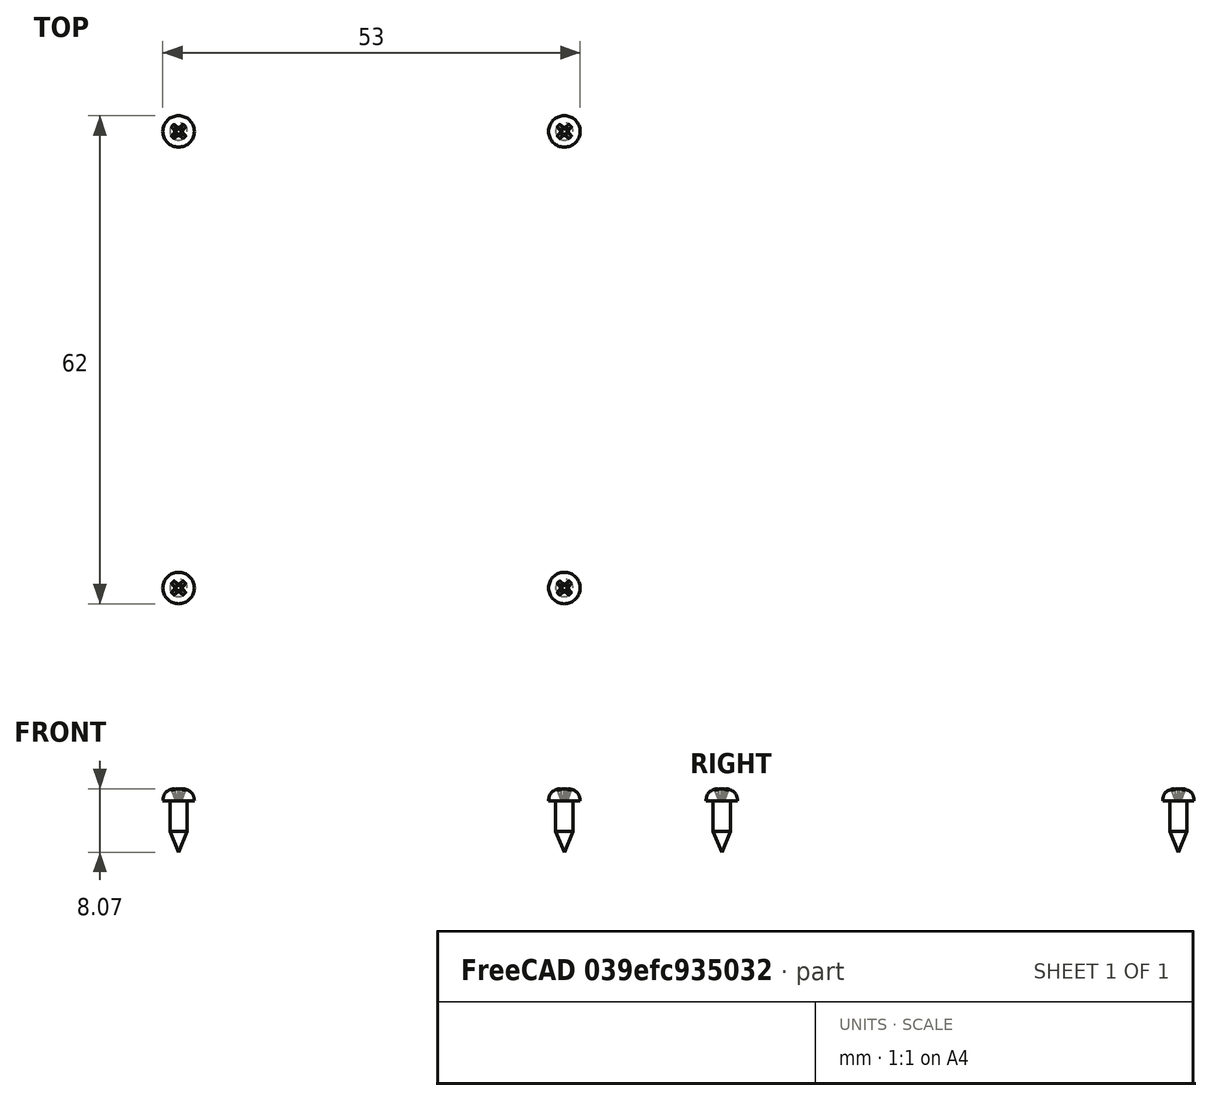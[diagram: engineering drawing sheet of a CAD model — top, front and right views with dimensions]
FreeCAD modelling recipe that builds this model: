
FCSTD DOCUMENT  (FreeCAD 1.0R39319 (Git))
Label: Assy_RaspberryPi5_carrier
License: All rights reserved
LicenseURL: https://en.wikipedia.org/wiki/All_rights_reserved
objects: TechDraw::DrawViewBalloon×6, Part::FeaturePython×4, TechDraw::DrawProjGroupItem×4, App::DocumentObjectGroup×3, TechDraw::DrawViewDimension×3, App::Link×2, TechDraw::DrawSVGTemplate×2, TechDraw::DrawPage×2, PartDesign::CoordinateSystem×1, App::FeaturePython×1, App::Part×1, Spreadsheet::Sheet×1, TechDraw::DrawViewSpreadsheet×1, TechDraw::DrawProjGroup×1
note: 11 computed .brp shape members not serialized (recipe doc carries the construction recipe); baked Part::Feature solids carry a one-line shape summary decoded from their .brp
EXTERNAL_REF file=../../Part/Print/Pi5_Carrier_vertical_3mm.FCStd obj=LCS_1
EXTERNAL_REF file=../../Part/Print/Pi5_Carrier_vertical_3mm.FCStd obj=Part
EXTERNAL_REF file=../../Part/Print/Pi5_Carrier_vertical_3mm.FCStd obj=pi5_att
EXTERNAL_REF file=../../Part/Purchase/RaspberryPi5.FCStd obj=LCS_1
EXTERNAL_REF file=../../Part/Purchase/RaspberryPi5.FCStd obj=RP_004882_DD___Pi_5_Mechanical_Reference_3D_model_Iss1

FEATURE [App::DocumentObjectGroup] Parts
FEATURE [PartDesign::CoordinateSystem] LCS_Origin
  AttacherType = Attacher::AttachEngine3D
  AttachmentSupport = -> [X_Axis]
  MapMode = 2
FEATURE [App::DocumentObjectGroup] Constraints
FEATURE [App::FeaturePython] Variables  # WARN: FeaturePython — macro-defined, semantics opaque (R4)
  Type = App::PropertyContainer
FEATURE [App::DocumentObjectGroup] Configurations
FEATURE [App::Link] Pi5_Carrier_vertical_3mm
  AttachedBy = #LCS_1
  AttachedTo = Parent Assembly#LCS_Origin
  LinkedObject = -> <external ../../Part/Print/Pi5_Carrier_vertical_3mm.FCStd>#Part
  SolverId = Asm4EE
  expr: Placement = LCS_Origin.Placement * AttachmentOffset * Pi5_Carrier_vertical_3mm#LCS_1.Placement ^ -1
FEATURE [App::Link] RP_004882_DD___Pi_5_Mechanical_Reference_3D_model_Iss1  label="RP-004882-DD - Pi 5 Mechanical Reference 3D model Iss1"
  AttachedBy = #LCS_1
  AttachedTo = Pi5_Carrier_vertical_3mm#pi5_att
  AttachmentOffset = pos=(0,0,0) rot=(0,0,1;3.14159rad)
  LinkPlacement = pos=(76,1,5.4) rot=(-0.57735,0.57735,0.57735;4.18879rad)
  LinkedObject = -> <external ../../Part/Purchase/RaspberryPi5.FCStd>#RP_004882_DD___Pi_5_Mechanical_Reference_3D_model_Iss1
  Placement = pos=(76,1,5.4) rot=(-0.57735,0.57735,0.57735;4.18879rad)
  SolverId = Asm4EE
  expr: Placement = Pi5_Carrier_vertical_3mm.Placement * Pi5_Carrier_vertical_3mm#pi5_att.Placement * AttachmentOffset * RaspberryPi5#LCS_1.Placement ^ -1
FEATURE [Part::FeaturePython] Screw  label="ST2.2x6.5-Screw"  # WARN: FeaturePython — macro-defined, semantics opaque (R4)
  BaseObject = -> Pi5_Carrier_vertical_3mm [Body.Fillet001.Edge193]
  Diameter = 1
  Invert = false
  LeftHanded = false
  Length = 1
  LengthCustom = 6.5
  MatchOuter = false
  Offset = 1.4
  OffsetAngle = 0
  Placement = pos=(51.5,40,6.9) rot=(0,0,1;0rad)
  Thread = false
  Type = 81
FEATURE [Part::FeaturePython] Screw001  label="ST2.2x6.5-Screw004"  # WARN: FeaturePython — macro-defined, semantics opaque (R4)
  BaseObject = -> Pi5_Carrier_vertical_3mm [Body.Fillet001.Edge195]
  Diameter = 1
  Invert = false
  LeftHanded = false
  Length = 1
  LengthCustom = 6.5
  MatchOuter = false
  Offset = 1.4
  OffsetAngle = 0
  Placement = pos=(100.5,40,6.9) rot=(0,0,1;0rad)
  Thread = false
  Type = 81
FEATURE [Part::FeaturePython] Screw002  label="ST2.2x6.5-Screw005"  # WARN: FeaturePython — macro-defined, semantics opaque (R4)
  BaseObject = -> Pi5_Carrier_vertical_3mm [Body.Fillet001.Edge169]
  Diameter = 1
  Invert = false
  LeftHanded = false
  Length = 1
  LengthCustom = 6.5
  MatchOuter = false
  Offset = 1.4
  OffsetAngle = 0
  Placement = pos=(51.5,-18,6.9) rot=(0,0,1;0rad)
  Thread = false
  Type = 81
FEATURE [Part::FeaturePython] Screw003  label="ST2.2x6.5-Screw006"  # WARN: FeaturePython — macro-defined, semantics opaque (R4)
  BaseObject = -> Pi5_Carrier_vertical_3mm [Body.Fillet001.Edge179]
  Diameter = 1
  Invert = false
  LeftHanded = false
  Length = 1
  LengthCustom = 6.5
  MatchOuter = false
  Offset = 1.4
  OffsetAngle = 0
  Placement = pos=(100.5,-18,6.9) rot=(0,0,1;0rad)
  Thread = false
  Type = 81
FEATURE [App::Part] Assembly  label="Assy_RaspberryPi5_carrier"
  AssemblyType = Part::Link
  Group = -> [LCS_Origin,Constraints,Variables,Configurations,Pi5_Carrier_vertical_3mm,RP_004882_DD___Pi_5_Mechanical_Reference_3D_model_Iss1,Screw,Screw001,Screw002,Screw003]
  Origin = -> Origin
  Type = Assembly
FEATURE [Spreadsheet::Sheet] Spreadsheet  label="BOM"
  cells = A1=3; B1=4; C1='M2x10 mm self-tapping screw; D1='8-12 mm ; A2=2; B2=1; C2='Pi5 ; D2='-; A3=1; B3=1; C3='Pi5_Carrier_vertical_3mm; D3='-; E3='PETG or PLA; A4='Position; B4='Quantity; C4='Part; D4='Dimensions; E4='Material
FEATURE [TechDraw::DrawSVGTemplate] Template
  EditableTexts = approval_person=GitHub PR; creator=Stefan; date_of_issue=20.03.2026; document_type=Assembly Drawing; general_tolerances=na; identification_number=na; language_code=EN; part_material=na; revision_index=AAA; scale=1 : 1; sheet_number=1 / 1; title=Assy_RaspberryPi5_carrier
  Height = 297
  Orientation = 0
  Template = <userpath>/Documents/PiTrac/3D Printed Parts/Enclosure Version 3/Assets/PiTrac_A4_Portrait_ISO5457_minimal.svg
  Width = 210
FEATURE [TechDraw::DrawViewSpreadsheet] Sheet
  CellEnd = E4
  CellStart = A1
  Font = osifont
  LineWidth = 0.35
  LockPosition = false
  Rotation = 0
  ScaleType = 2
  Source = -> Spreadsheet
  Symbol = <blob: 4580 chars omitted>
  TextSize = 12
  X = 117.534
  Y = 84.9956
FEATURE [TechDraw::DrawProjGroupItem] View
  CoarseView = false
  Direction = (0.57735,-0.57735,0.57735)
  Focus = 100
  HardHidden = false
  IsoCount = 0
  IsoHidden = false
  IsoVisible = false
  LockPosition = false
  Perspective = false
  Rotation = 0
  RotationVector = (1,0,0)
  Scale = 0.5
  ScaleType = 2
  ScrubCount = 1
  SeamHidden = false
  SeamVisible = false
  SmoothHidden = false
  SmoothVisible = true
  Source = -> [Assembly]
  Type = 0
  X = 160.566
  XDirection = (0.707107,0.707107,0)
  Y = 132.206
FEATURE [TechDraw::DrawProjGroupItem] View001  label="Front"
  CoarseView = false
  Direction = (0,0,1)
  Focus = 100
  HardHidden = false
  IsoCount = 0
  IsoHidden = false
  IsoVisible = false
  LockPosition = true
  Perspective = false
  Rotation = 0
  RotationVector = (1,0,0)
  ScaleType = 2
  ScrubCount = 1
  SeamHidden = false
  SeamVisible = false
  SmoothHidden = false
  SmoothVisible = true
  Source = -> [Assembly]
  Type = 0
  X = 0
  XDirection = (1,0,0)
  Y = 0
FEATURE [TechDraw::DrawProjGroupItem] ProjItem  label="Left"
  CoarseView = false
  Direction = (-1,0,1e-16)
  Focus = 100
  HardHidden = false
  IsoCount = 0
  IsoHidden = false
  IsoVisible = false
  LockPosition = false
  Perspective = false
  Rotation = 0
  RotationVector = (1,0,0)
  ScaleType = 0
  ScrubCount = 1
  SeamHidden = false
  SeamVisible = false
  SmoothHidden = false
  SmoothVisible = true
  Source = -> [Assembly]
  Type = 1
  X = 81.675
  XDirection = (1e-16,0,1)
  Y = 0
FEATURE [TechDraw::DrawProjGroup] ProjGroup
  Anchor = -> View001
  AutoDistribute = true
  LockPosition = false
  ProjectionType = 0
  Rotation = 0
  ScaleType = 0
  Source = -> [Assembly]
  Views = -> [View001,ProjItem]
  X = 86.1994
  Y = 225.791
  spacingX = 15
  spacingY = 15
FEATURE [TechDraw::DrawViewBalloon] Balloon
  BubbleShape = 0
  EndType = 0
  EndTypeScale = 1
  KinkLength = 5
  LockPosition = false
  OriginX = -31.4686
  OriginY = -41.9631
  Rotation = 0
  ScaleType = 0
  ShapeScale = 1
  SourceView = -> View001
  Text = 1
  TextWrapLen = -1
  X = -43.2208
  Y = -65
FEATURE [TechDraw::DrawViewBalloon] Balloon001
  BubbleShape = 0
  EndType = 0
  EndTypeScale = 1
  KinkLength = 5
  LockPosition = false
  OriginX = 16.1596
  OriginY = -10.6287
  Rotation = 0
  ScaleType = 0
  ShapeScale = 1
  SourceView = -> Balloon
  Text = 2
  TextWrapLen = -1
  X = 18.1946
  Y = -65
FEATURE [TechDraw::DrawViewBalloon] Balloon002
  BubbleShape = 0
  EndType = 0
  EndTypeScale = 1
  KinkLength = 5
  LockPosition = false
  OriginX = -3.47658
  OriginY = -19.4023
  Rotation = 0
  ScaleType = 0
  ShapeScale = 1
  SourceView = -> Balloon001
  Text = 3
  TextWrapLen = -1
  X = -15.2288
  Y = -65
FEATURE [TechDraw::DrawViewBalloon] Balloon003
  BubbleShape = 0
  EndType = 0
  EndTypeScale = 1
  KinkLength = 5
  LockPosition = false
  OriginX = 45.8229
  OriginY = -18.9845
  Rotation = 0
  ScaleType = 0
  ShapeScale = 1
  SourceView = -> Balloon002
  Text = 3
  TextWrapLen = -1
  X = 40.3376
  Y = -65
FEATURE [TechDraw::DrawViewBalloon] Balloon004
  BubbleShape = 0
  EndType = 0
  EndTypeScale = 1
  KinkLength = 5
  LockPosition = false
  OriginX = -3.05879
  OriginY = 38.6707
  Rotation = 0
  ScaleType = 0
  ShapeScale = 1
  SourceView = -> View001
  Text = 3
  TextWrapLen = -1
  X = -18.1533
  Y = 53
FEATURE [TechDraw::DrawViewBalloon] Balloon005
  BubbleShape = 0
  EndType = 0
  EndTypeScale = 1
  KinkLength = 5
  LockPosition = false
  OriginX = 45.4051
  OriginY = 39.9241
  Rotation = 0
  ScaleType = 0
  ShapeScale = 1
  SourceView = -> Balloon004
  Text = 3
  TextWrapLen = -1
  X = 32.3995
  Y = 53
FEATURE [TechDraw::DrawViewDimension] Dimension
  AngleOverride = false
  Arbitrary = false
  ArbitraryTolerances = false
  BoxCorners = (2) [(-55,-45,-1e-07),(55,45,1e-07)]
  EqualTolerance = true
  ExtensionAngle = 0
  FormatSpec = %.2w
  FormatSpecOverTolerance = %+.2w
  FormatSpecUnderTolerance = %+.2w
  Inverted = false
  LineAngle = 0
  LockPosition = false
  MeasureType = 1
  OverTolerance = 0
  References2D = -> [View001]
  Rotation = 0
  ScaleType = 0
  TheoreticalExact = false
  Type = 0
  UnderTolerance = 0
  X = 8.83117
  Y = -68.9029
FEATURE [TechDraw::DrawViewDimension] Dimension001
  AngleOverride = false
  Arbitrary = false
  ArbitraryTolerances = false
  BoxCorners = (2) [(-55,-45,-1e-07),(55,45,1e-07)]
  EqualTolerance = true
  ExtensionAngle = 0
  FormatSpec = %.2w
  FormatSpecOverTolerance = %+.2w
  FormatSpecUnderTolerance = %+.2w
  Inverted = false
  LineAngle = 0
  LockPosition = false
  MeasureType = 1
  OverTolerance = 0
  References2D = -> [View001]
  Rotation = 0
  ScaleType = 0
  TheoreticalExact = false
  Type = 0
  UnderTolerance = 0
  X = 101.118
  Y = -0.2
FEATURE [TechDraw::DrawViewDimension] Dimension002
  AngleOverride = false
  Arbitrary = false
  ArbitraryTolerances = false
  BoxCorners = (2) [(-11.675,-45,-1e-07),(11.675,45,1e-07)]
  EqualTolerance = true
  ExtensionAngle = 0
  FormatSpec = %.2w
  FormatSpecOverTolerance = %+.2w
  FormatSpecUnderTolerance = %+.2w
  Inverted = false
  LineAngle = 0
  LockPosition = false
  MeasureType = 1
  OverTolerance = 0
  References2D = -> [ProjItem]
  Rotation = 0
  ScaleType = 0
  TheoreticalExact = false
  Type = 0
  UnderTolerance = 0
  X = -0.525
  Y = -60.4861
FEATURE [TechDraw::DrawPage] Page
  KeepUpdated = true
  NextBalloonIndex = 7
  ProjectionType = 0
  Template = -> Template
  Views = -> [Sheet,View,ProjGroup,Balloon,Balloon001,Balloon002,Balloon003,Balloon004,Balloon005,Dimension,Dimension001,Dimension002]
FEATURE [TechDraw::DrawSVGTemplate] Template001
  Height = 210
  Orientation = 1
  Template = C:/Program Files/FreeCAD 1.0/data/Mod/TechDraw/Templates/Default_Template_A4_Landscape.svg
  Width = 297
FEATURE [TechDraw::DrawProjGroupItem] View002
  CoarseView = false
  Direction = (0.57735,-0.57735,0.57735)
  Focus = 100
  HardHidden = false
  IsoCount = 0
  IsoHidden = false
  IsoVisible = false
  LockPosition = false
  Perspective = false
  Rotation = 0
  RotationVector = (1,0,0)
  Scale = 2
  ScaleType = 2
  ScrubCount = 1
  SeamHidden = false
  SeamVisible = false
  SmoothHidden = false
  SmoothVisible = true
  Source = -> [Assembly]
  Type = 0
  X = 148.5
  XDirection = (0.707107,0.707107,0)
  Y = 105
FEATURE [TechDraw::DrawPage] Page001
  KeepUpdated = true
  NextBalloonIndex = 1
  ProjectionType = 0
  Template = -> Template001
  Views = -> [View002]

RESOLVED EXTERNAL PARTS (link-assembly join: the EXTERNAL_REF files above that resolve inside this repo's crawl, each included once):
---- part ../../Part/Print/Pi5_Carrier_vertical_3mm.FCStd = doc fcstd_1f498473da96 ----
FCSTD DOCUMENT  (FreeCAD 1.0R39319 (Git))
Label: Pi5_Carrier_vertical_3mm
License: All rights reserved
LicenseURL: https://en.wikipedia.org/wiki/All_rights_reserved
objects: Sketcher::SketchObject×7, PartDesign::Pocket×5, PartDesign::LinearPattern×4, PartDesign::Pad×2, PartDesign::MultiTransform×2, PartDesign::Fillet×2, PartDesign::CoordinateSystem×2, PartDesign::Mirrored×1, PartDesign::Body×1, App::Part×1
note: 58 computed .brp shape members not serialized (recipe doc carries the construction recipe); baked Part::Feature solids carry a one-line shape summary decoded from their .brp

FEATURE [Sketcher::SketchObject] Sketch
  ArcFitTolerance = 1e-06
  AttachmentSupport = -> [XY_Plane001]
  FullyConstrained = true
  MakeInternals = false
  MapMode = 5
  sketch-geometry (4):
    g0: LineSegment StartX=0 StartY=44.5 StartZ=0 EndX=0 EndY=-44.5 EndZ=0
    g1: LineSegment StartX=0 StartY=-44.5 StartZ=0 EndX=110 EndY=-44.5 EndZ=0
    g2: LineSegment StartX=110 StartY=-44.5 StartZ=0 EndX=110 EndY=44.5 EndZ=0
    g3: LineSegment StartX=110 StartY=44.5 StartZ=0 EndX=0 EndY=44.5 EndZ=0
  constraints (11):
    c: Coincident(g0,g1)
    c: Coincident(g1,g2)
    c: Coincident(g2,g3)
    c: Coincident(g3,g0)
    c: Vertical(g2)
    c: Horizontal(g1)
    c: Horizontal(g3)
    c: PointOnObject(g0,g-2)
    c: Distance(g1,g3) = 89
    c: Distance(g2,g0) = 110
    c: Symmetric(g0,g0,g-1)
FEATURE [PartDesign::Pad] Pad
  Direction = (0,0,1)
  Length = 2.5
  Length2 = 10
  Profile = -> Sketch
  ReferenceAxis = -> Sketch [N_Axis]
  Refine = true
  Suppressed = false
  Type = 0
FEATURE [Sketcher::SketchObject] Sketch001
  ArcFitTolerance = 1e-06
  AttachmentSupport = -> [Pad]
  ExternalGeometry = -> [Pad]
  FullyConstrained = true
  MakeInternals = false
  MapMode = 5
  Placement = pos=(0,0,2.5) rot=(0,0,1;0rad)
  sketch-geometry (8):
    g0: LineSegment [constr] StartX=51.5 StartY=40 StartZ=0 EndX=51.5 EndY=-18 EndZ=0
    g1: LineSegment [constr] StartX=51.5 StartY=-18 StartZ=0 EndX=100.5 EndY=-18 EndZ=0
    g2: LineSegment [constr] StartX=100.5 StartY=-18 StartZ=0 EndX=100.5 EndY=40 EndZ=0
    g3: LineSegment [constr] StartX=100.5 StartY=40 StartZ=0 EndX=51.5 EndY=40 EndZ=0
    g4: Circle CenterX=100.5 CenterY=40 CenterZ=0 NormalX=0 NormalY=0 NormalZ=1 AngleXU=0 Radius=2.9
    g5: Circle CenterX=100.5 CenterY=-18 CenterZ=0 NormalX=0 NormalY=0 NormalZ=1 AngleXU=0 Radius=2.9
    g6: Circle CenterX=51.5 CenterY=40 CenterZ=0 NormalX=0 NormalY=0 NormalZ=1 AngleXU=0 Radius=2.9
    g7: Circle CenterX=51.5 CenterY=-18 CenterZ=0 NormalX=0 NormalY=0 NormalZ=1 AngleXU=0 Radius=2.9
  constraints (20):
    c: Coincident(g0,g1)
    c: Coincident(g1,g2)
    c: Coincident(g2,g3)
    c: Coincident(g3,g0)
    c: Vertical(g0)
    c: Vertical(g2)
    c: Horizontal(g1)
    c: Horizontal(g3)
    c: Coincident(g4,g2)
    c: Coincident(g5,g1)
    c: Coincident(g6,g0)
    c: Coincident(g7,g0)
    c: Distance(g-3,g2) = 9.5
    c: Distance(g1,g3) = 58
    c: Distance(g0,g2) = 49
    c: Diameter(g7) = 5.8
    c: Diameter(g6) = 5.8
    c: Diameter(g4) = 5.8
    c: Diameter(g5) = 5.8
    c: Distance(g-4,g3) = 4.5
FEATURE [PartDesign::Pad] Pad001
  BaseFeature = -> Pad
  Direction = (0,0,1)
  Length = 3
  Length2 = 10
  Profile = -> Sketch001
  ReferenceAxis = -> Sketch001 [N_Axis]
  Refine = true
  Suppressed = false
  Type = 0
FEATURE [Sketcher::SketchObject] Sketch002
  ArcFitTolerance = 1e-06
  AttachmentSupport = -> [Pad001]
  ExternalGeometry = -> [Pad001]
  FullyConstrained = true
  MakeInternals = false
  MapMode = 5
  Placement = pos=(0,0,5.5) rot=(0,0,1;0rad)
  sketch-geometry (4):
    g0: Circle CenterX=51.5 CenterY=40 CenterZ=0 NormalX=0 NormalY=0 NormalZ=1 AngleXU=0 Radius=1
    g1: Circle CenterX=100.5 CenterY=40 CenterZ=0 NormalX=0 NormalY=0 NormalZ=1 AngleXU=0 Radius=1
    g2: Circle CenterX=51.5 CenterY=-18 CenterZ=0 NormalX=0 NormalY=0 NormalZ=1 AngleXU=0 Radius=1
    g3: Circle CenterX=100.5 CenterY=-18 CenterZ=0 NormalX=0 NormalY=0 NormalZ=1 AngleXU=0 Radius=1
  constraints (8):
    c: Coincident(g0,g-4)
    c: Coincident(g1,g-3)
    c: Coincident(g2,g-5)
    c: Coincident(g3,g-6)
    c: Diameter(g0) = 2
    c: Diameter(g1) = 2
    c: Diameter(g2) = 2
    c: Diameter(g3) = 2
FEATURE [PartDesign::Pocket] Pocket
  BaseFeature = -> Pad001
  Direction = (0,0,-1)
  Length = 5
  Length2 = 5
  Profile = -> Sketch002
  ReferenceAxis = -> Sketch002 [N_Axis]
  Refine = true
  Suppressed = false
  Type = 1
FEATURE [Sketcher::SketchObject] Sketch003
  ArcFitTolerance = 1e-06
  ExternalGeometry = -> [Pocket]
  FullyConstrained = true
  MakeInternals = false
  MapMode = 5
  Placement = pos=(0,0,2.5) rot=(0,0,1;0rad)
  sketch-geometry (5):
    g0: LineSegment StartX=66 StartY=44.5 StartZ=0 EndX=66 EndY=24.5 EndZ=0
    g1: LineSegment StartX=66 StartY=24.5 StartZ=0 EndX=86 EndY=24.5 EndZ=0
    g2: LineSegment StartX=86 StartY=24.5 StartZ=0 EndX=86 EndY=44.5 EndZ=0
    g3: LineSegment StartX=86 StartY=44.5 StartZ=0 EndX=66 EndY=44.5 EndZ=0
    g4: LineSegment [constr] StartX=76 StartY=44.5 StartZ=0 EndX=76 EndY=24.5 EndZ=0
  constraints (13):
    c: Coincident(g0,g1)
    c: Coincident(g1,g2)
    c: Coincident(g2,g3)
    c: Coincident(g3,g0)
    c: Vertical(g0)
    c: Horizontal(g1)
    c: Horizontal(g3)
    c: DistanceY(g0,g0) = 20
    c: DistanceX(g3,g3) = 20
    c: Symmetric(g3,g3,g4)
    c: Symmetric(g1,g1,g4)
    c: PointOnObject(g2,g-3)
    c: Symmetric(g-4,g-5,g4)
FEATURE [PartDesign::Pocket] Pocket001
  BaseFeature = -> Pocket
  Direction = (0,0,-1)
  Length = 5
  Length2 = 5
  Profile = -> Sketch003
  ReferenceAxis = -> Sketch003 [N_Axis]
  Refine = true
  Suppressed = false
  Type = 1
FEATURE [Sketcher::SketchObject] Sketch004
  ArcFitTolerance = 1e-06
  AttachmentSupport = -> [Pocket001]
  ExternalGeometry = -> [Pocket001]
  FullyConstrained = true
  MakeInternals = false
  MapMode = 5
  Placement = pos=(0,0,2.5) rot=(0,0,1;0rad)
  sketch-geometry (5):
    g0: ArcOfCircle CenterX=76 CenterY=15.5 CenterZ=0 NormalX=0 NormalY=0 NormalZ=1 AngleXU=0 Radius=4 StartAngle=1e-16 EndAngle=3.14159
    g1: ArcOfCircle CenterX=76 CenterY=-35.5 CenterZ=0 NormalX=0 NormalY=0 NormalZ=1 AngleXU=0 Radius=4 StartAngle=3.14159 EndAngle=6.28319
    g2: LineSegment StartX=80 StartY=15.5 StartZ=0 EndX=80 EndY=-35.5 EndZ=0
    g3: LineSegment StartX=72 StartY=15.5 StartZ=0 EndX=72 EndY=-35.5 EndZ=0
    g4: LineSegment [constr] StartX=76 StartY=15.5 StartZ=0 EndX=76 EndY=-35.5 EndZ=0
  constraints (11):
    c: Tangent(g0,g2) = 1.5708
    c: Tangent(g0,g3) = -1.5708
    c: Tangent(g1,g2) = 1.5708
    c: Tangent(g1,g3) = -1.5708
    c: Equal(g0,g1)
    c: Distance(g0,g-3) = 5
    c: Radius(g1) = 4
    c: Coincident(g4,g0)
    c: Coincident(g4,g1)
    c: Symmetric(g-3,g-3,g4)
    c: Distance(g1,g-4) = 5
FEATURE [PartDesign::Pocket] Pocket002
  BaseFeature = -> Pocket001
  Direction = (0,0,-1)
  Length = 5
  Length2 = 5
  Profile = -> Sketch004
  ReferenceAxis = -> Sketch004 [N_Axis]
  Refine = true
  Suppressed = false
  Type = 1
FEATURE [PartDesign::LinearPattern] LinearPattern
  Direction = -> Sketch004 [H_Axis]
  Length = 16
  Mode = 1
  Occurrences = 2
  Offset = 16
  Refine = true
  Suppressed = false
  TransformMode = 0
FEATURE [PartDesign::LinearPattern] LinearPattern001
  Direction = -> Sketch004 [H_Axis]
  Length = 16
  Mode = 1
  Occurrences = 2
  Offset = 16
  Refine = true
  Reversed = true
  Suppressed = false
  TransformMode = 0
FEATURE [PartDesign::MultiTransform] MultiTransform
  BaseFeature = -> Pocket002
  Originals = -> [Pocket002]
  Refine = true
  Suppressed = false
  TransformMode = 0
  Transformations = -> [LinearPattern,LinearPattern001]
FEATURE [Sketcher::SketchObject] Sketch005
  ArcFitTolerance = 1e-06
  AttachmentSupport = -> [MultiTransform]
  ExternalGeometry = -> [MultiTransform]
  FullyConstrained = true
  MakeInternals = false
  MapMode = 5
  Placement = pos=(0,0,2.5) rot=(0,0,1;0rad)
  sketch-geometry (5):
    g0: ArcOfCircle CenterX=9 CenterY=0 CenterZ=0 NormalX=0 NormalY=0 NormalZ=1 AngleXU=0 Radius=4 StartAngle=1.5708 EndAngle=4.71239
    g1: ArcOfCircle CenterX=43 CenterY=-1e-16 CenterZ=0 NormalX=0 NormalY=0 NormalZ=1 AngleXU=0 Radius=4 StartAngle=4.71239 EndAngle=7.85398
    g2: LineSegment StartX=9 StartY=4 StartZ=0 EndX=43 EndY=4 EndZ=0
    g3: LineSegment StartX=9 StartY=-4 StartZ=0 EndX=43 EndY=-4 EndZ=0
    g4: LineSegment [constr] StartX=51.5 StartY=40 StartZ=0 EndX=51.5 EndY=-18 EndZ=0
  constraints (12):
    c: Tangent(g0,g2) = 1.5708
    c: Tangent(g0,g3) = -1.5708
    c: Tangent(g1,g2) = 1.5708
    c: Tangent(g1,g3) = -1.5708
    c: Equal(g0,g1)
    c: Horizontal(g3)
    c: PointOnObject(g0,g-1)
    c: Radius(g0) = 4
    c: Distance(g0,g-2) = 5
    c: Coincident(g4,g-5)
    c: Coincident(g4,g-3)
    c: Distance(g1,g4) = 4.5
FEATURE [PartDesign::Pocket] Pocket003
  BaseFeature = -> MultiTransform
  Direction = (0,0,-1)
  Length = 5
  Length2 = 5
  Profile = -> Sketch005
  ReferenceAxis = -> Sketch005 [N_Axis]
  Refine = true
  Suppressed = false
  Type = 1
FEATURE [PartDesign::LinearPattern] LinearPattern002
  Direction = -> Y_Axis001
  Length = 32
  Mode = 1
  Occurrences = 3
  Offset = 16
  Refine = true
  Suppressed = false
  TransformMode = 0
FEATURE [PartDesign::LinearPattern] LinearPattern003
  Direction = -> Y_Axis001
  Length = 32
  Mode = 1
  Occurrences = 3
  Offset = 16
  Refine = true
  Reversed = true
  Suppressed = false
  TransformMode = 0
FEATURE [PartDesign::MultiTransform] MultiTransform001
  BaseFeature = -> Pocket003
  Originals = -> [Pocket003]
  Refine = true
  Suppressed = false
  TransformMode = 0
  Transformations = -> [LinearPattern002,LinearPattern003]
FEATURE [PartDesign::Fillet] Fillet
  Base = -> MultiTransform001 [Edge94,Edge7,Edge93,Edge8,Edge96,Edge95,Edge1,Edge2]
  BaseFeature = -> MultiTransform001
  Radius = 3.5
  Refine = true
  SupportTransform = false
  Suppressed = false
  UseAllEdges = false
FEATURE [Sketcher::SketchObject] Sketch006
  ArcFitTolerance = 1e-06
  AttachmentSupport = -> [Fillet]
  ExternalGeometry = -> [Fillet]
  FullyConstrained = true
  MakeInternals = false
  MapMode = 5
  Placement = pos=(0,0,2.5) rot=(0,0,1;0rad)
  sketch-geometry (8):
    g0: LineSegment StartX=6 StartY=44.5 StartZ=0 EndX=0 EndY=44.5 EndZ=0
    g1: LineSegment StartX=0 StartY=44.5 StartZ=0 EndX=0 EndY=38.5 EndZ=0
    g2: LineSegment StartX=0 StartY=38.5 StartZ=0 EndX=6 EndY=38.5 EndZ=0
    g3: LineSegment StartX=6 StartY=38.5 StartZ=0 EndX=6 EndY=44.5 EndZ=0
    g4: LineSegment StartX=104 StartY=44.5 StartZ=0 EndX=104 EndY=38.5 EndZ=0
    g5: LineSegment StartX=104 StartY=38.5 StartZ=0 EndX=110 EndY=38.5 EndZ=0
    g6: LineSegment StartX=110 StartY=38.5 StartZ=0 EndX=110 EndY=44.5 EndZ=0
    g7: LineSegment StartX=110 StartY=44.5 StartZ=0 EndX=104 EndY=44.5 EndZ=0
  constraints (24):
    c: Coincident(g0,g1)
    c: Coincident(g1,g2)
    c: Coincident(g2,g3)
    c: Coincident(g3,g0)
    c: Horizontal(g0)
    c: Horizontal(g2)
    c: Vertical(g1)
    c: Vertical(g3)
    c: PointOnObject(g0,g-5)
    c: PointOnObject(g1,g-2)
    c: Coincident(g4,g5)
    c: Coincident(g5,g6)
    c: Coincident(g6,g7)
    c: Coincident(g7,g4)
    c: Vertical(g4)
    c: Vertical(g6)
    c: Horizontal(g5)
    c: Horizontal(g7)
    c: PointOnObject(g4,g-3)
    c: PointOnObject(g5,g-4)
    c: DistanceY(g6,g6) = 6
    c: DistanceX(g7,g7) = 6
    c: DistanceX(g0,g0) = 6
    c: Distance(g3,g3) = 6
FEATURE [PartDesign::Pocket] Pocket004
  BaseFeature = -> Fillet
  Direction = (0,0,-1)
  Length = 5
  Length2 = 5
  Profile = -> Sketch006
  ReferenceAxis = -> Sketch006 [N_Axis]
  Refine = true
  Suppressed = false
  Type = 1
FEATURE [PartDesign::Mirrored] Mirrored
  BaseFeature = -> Pocket004
  MirrorPlane = -> XZ_Plane001
  Originals = -> [Pocket004]
  Refine = true
  Suppressed = false
  TransformMode = 0
FEATURE [PartDesign::Fillet] Fillet001
  Base = -> Mirrored [Edge132,Edge4,Edge125,Edge127,Edge128,Edge130,Edge131,Edge2]
  BaseFeature = -> Mirrored
  Radius = 3.5
  Refine = true
  SupportTransform = false
  Suppressed = false
  UseAllEdges = false
FEATURE [PartDesign::Body] Body  label="Pi5_Carrier_vertical_3mm001"
  AllowCompound = false
  Group = -> [Sketch,Pad,Sketch001,Pad001,Sketch002,Pocket,Sketch003,Pocket001,Sketch004,Pocket002,MultiTransform,LinearPattern,LinearPattern001,Sketch005,Pocket003,MultiTransform001,LinearPattern002,LinearPattern003,Fillet,Sketch006,Pocket004,Mirrored,Fillet001]
  Origin = -> Origin001
  Tip = -> Fillet001
FEATURE [PartDesign::CoordinateSystem] LCS_1
  AttacherType = Attacher::AttachEngine3D
FEATURE [PartDesign::CoordinateSystem] pi5_att
  AttacherType = Attacher::AttachEngine3D
  AttachmentSupport = -> [Fillet001]
  MapMode = 11
  Placement = pos=(100.5,40,5.5) rot=(0,0,1;1.5708rad)
FEATURE [App::Part] Part  label="Pi5_Carrier_vertical_3mm"
  Group = -> [Body,LCS_1,pi5_att]
  Origin = -> Origin
